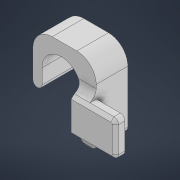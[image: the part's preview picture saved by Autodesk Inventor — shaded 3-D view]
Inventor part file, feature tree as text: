
AUTODESK INVENTOR PART (.ipt)
format: ipt  version: 2022 (Build 260153000, 153)  size: 192,000 bytes
history: native  units: mm
features: extrude x4, sketch x4, fillet x3, chamfer x1
ambient origin geometry x8: Origin, YZ Plane, XZ Plane, XY Plane, X Axis, Y Axis, Z Axis, Center Point
bodies: Solid1 (feature_tree)
feature tree (12):
  extrude  "Extrusion1"  Depth=18.0mm
  extrude  "Extrusion2"  Depth=10.0mm
  extrude  "Extrusion3"  Depth=2.0mm
  extrude  "Extrusion4"  Depth=10.0mm TaperAngle=0.0deg
  fillet  "Fillet3"  Radius=2.75mm
  fillet  "Fillet4"  Radius=2.5mm
  chamfer  "Chamfer1"  Distance=14.0mm
  fillet  "Fillet6"  Radius=3.0mm
  sketch  "Sketch1"  dims[d0=12.2mm d1=18.0mm]
  sketch  "Sketch2"  dims[d2=10.0mm d3=0.0mm d4=4.0mm]
  sketch  "Sketch3"  dims[d7=5.0mm d8=2.0mm]
  sketch  "Sketch5"  dims[d9=3.2mm d10=10.0mm d11=0.0mm d13=2.75mm d14=2.5mm d15=0.0mm d18=14.0mm d19=3.0mm d20=0.0mm d21=6.1mm d22=1.45mm d24=1.0mm d25=2.0mm d26=45.0deg d27=3.0mm d28=2.0mm]
